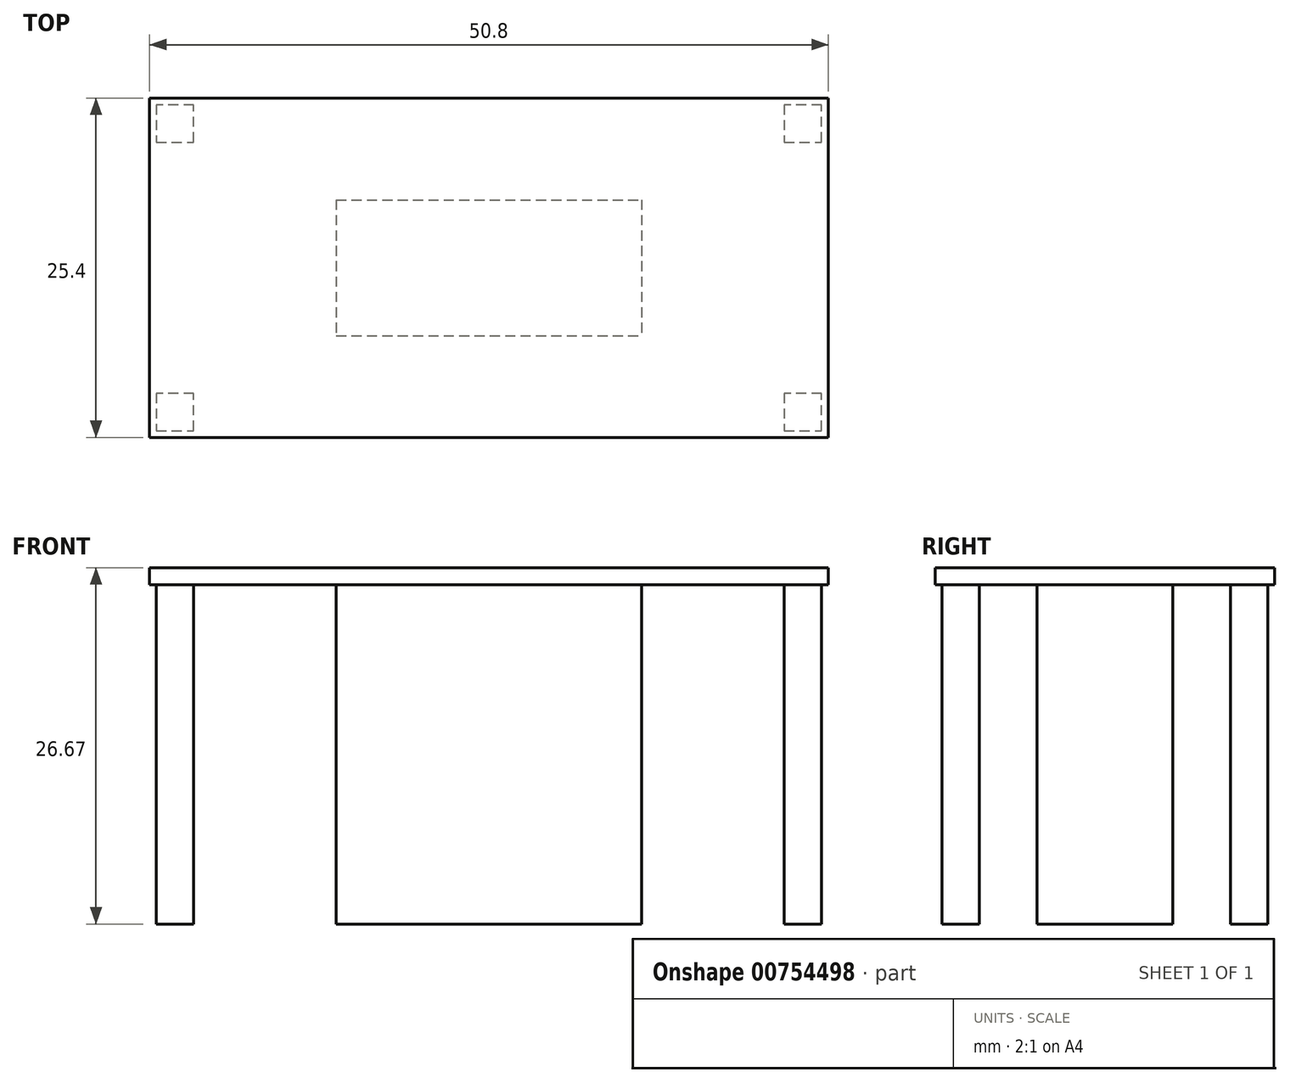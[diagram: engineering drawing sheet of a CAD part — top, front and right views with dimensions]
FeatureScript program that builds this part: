
annotation { "Feature Type Name" : "Feature", "Feature Type Description" : "" }
export const myFeature = defineFeature(function(context is Context, id is Id, definition is map)
    precondition{}
    {
        {
            var Q0;
            Q0=qCreatedBy(makeId("Top.planeOp"),FACE);
            var sketch = newSketch(context, id + "F0", { "sketchPlane" : qUnion([Q0])});
            skLineSegment(sketch, "E0.bottom", {"start": v(25.4, -12.7) * mm, "end": v(-25.4, -12.7) * mm});
            skLineSegment(sketch, "E0.top", {"start": v(25.4, 12.7) * mm, "end": v(-25.4, 12.7) * mm});
            skLineSegment(sketch, "E0.left", {"start": v(25.4, -12.7) * mm, "end": v(25.4, 12.7) * mm});
            skLineSegment(sketch, "E0.right", {"start": v(-25.4, -12.7) * mm, "end": v(-25.4, 12.7) * mm});
            skPoint(sketch, "E0.middle", {"position": v(0, 0) * mm});
            skLineSegment(sketch, "E1.bottom", {"start": v(-25.4, 12.7) * mm, "end": v(-21.6, 12.7) * mm});
            skLineSegment(sketch, "E1.top", {"start": v(-25.4, 8.9) * mm, "end": v(-21.59, 8.9) * mm});
            skLineSegment(sketch, "E1.left", {"start": v(-25.4, 12.7) * mm, "end": v(-25.4, 8.9) * mm});
            skLineSegment(sketch, "E1.right", {"start": v(-21.6, 12.7) * mm, "end": v(-21.6, 8.9) * mm});
            skLineSegment(sketch, "E2.bottom", {"start": v(-25.4, -12.7) * mm, "end": v(-21.6, -12.7) * mm});
            skLineSegment(sketch, "E2.top", {"start": v(-25.4, -8.89) * mm, "end": v(-21.6, -8.89) * mm});
            skLineSegment(sketch, "E2.left", {"start": v(-25.4, -12.7) * mm, "end": v(-25.4, -8.89) * mm});
            skLineSegment(sketch, "E2.right", {"start": v(-21.6, -12.7) * mm, "end": v(-21.6, -8.89) * mm});
            skLineSegment(sketch, "E3.bottom", {"start": v(25.4, -12.7) * mm, "end": v(21.59, -12.7) * mm});
            skLineSegment(sketch, "E3.top", {"start": v(25.4, -8.89) * mm, "end": v(21.59, -8.89) * mm});
            skLineSegment(sketch, "E3.left", {"start": v(25.4, -12.7) * mm, "end": v(25.4, -8.89) * mm});
            skLineSegment(sketch, "E3.right", {"start": v(21.59, -12.7) * mm, "end": v(21.59, -8.89) * mm});
            skLineSegment(sketch, "E4.bottom", {"start": v(25.4, 12.7) * mm, "end": v(21.59, 12.7) * mm});
            skLineSegment(sketch, "E4.top", {"start": v(25.4, 8.9) * mm, "end": v(21.6, 8.9) * mm});
            skLineSegment(sketch, "E4.left", {"start": v(25.4, 12.7) * mm, "end": v(25.4, 8.9) * mm});
            skLineSegment(sketch, "E4.right", {"start": v(21.59, 12.7) * mm, "end": v(21.59, 8.9) * mm});
            skLineSegment(sketch, "E5.bottom", {"start": v(-11.43, 5.08) * mm, "end": v(11.43, 5.08) * mm});
            skLineSegment(sketch, "E5.top", {"start": v(-11.43, -5.08) * mm, "end": v(11.43, -5.08) * mm});
            skLineSegment(sketch, "E5.left", {"start": v(-11.43, 5.08) * mm, "end": v(-11.43, -5.08) * mm});
            skLineSegment(sketch, "E5.right", {"start": v(11.43, 5.08) * mm, "end": v(11.43, -5.08) * mm});
            skSolve(sketch);
        }
        {
            var Q0;
            {var subQ4=sQuery(id+"F0.wireOp",EDGE,"E2.top");Q0=makeQuery(id+"F0.imprint","IMPRINT",FACE,{"disambiguationData":[TD([[makeQuery(id+"F0.imprint","IMPRINT",EDGE,{"derivedFrom":subQ4}),-1.0]])]});}
            var sketch = newSketch(context, id + "F1", { "sketchPlane" : qUnion([Q0])});
            skLineSegment(sketch, "E6.0", {"start": v(-24.9, -12.2) * mm, "end": v(-22.1, -12.2) * mm});
            skLineSegment(sketch, "E6.1", {"start": v(-24.9, -9.4) * mm, "end": v(-24.9, -12.2) * mm});
            skLineSegment(sketch, "E6.2", {"start": v(-22.1, -9.4) * mm, "end": v(-24.9, -9.4) * mm});
            skLineSegment(sketch, "E6.3", {"start": v(-22.1, -12.2) * mm, "end": v(-22.1, -9.4) * mm});
            skLineSegment(sketch, "E7.0", {"start": v(22.1, -9.4) * mm, "end": v(22.1, -12.2) * mm});
            skLineSegment(sketch, "E7.1", {"start": v(24.9, -9.4) * mm, "end": v(22.1, -9.4) * mm});
            skLineSegment(sketch, "E7.2", {"start": v(24.9, -12.2) * mm, "end": v(24.9, -9.4) * mm});
            skLineSegment(sketch, "E7.3", {"start": v(22.1, -12.2) * mm, "end": v(24.9, -12.2) * mm});
            skLineSegment(sketch, "E8.0", {"start": v(24.9, 9.4) * mm, "end": v(24.9, 12.2) * mm});
            skLineSegment(sketch, "E8.1", {"start": v(22.1, 9.4) * mm, "end": v(24.9, 9.4) * mm});
            skLineSegment(sketch, "E8.2", {"start": v(22.1, 12.2) * mm, "end": v(22.1, 9.4) * mm});
            skLineSegment(sketch, "E8.3", {"start": v(24.9, 12.2) * mm, "end": v(22.1, 12.2) * mm});
            skLineSegment(sketch, "E9.0", {"start": v(-22.1, 12.2) * mm, "end": v(-24.9, 12.2) * mm});
            skLineSegment(sketch, "E9.1", {"start": v(-22.1, 9.4) * mm, "end": v(-22.1, 12.2) * mm});
            skLineSegment(sketch, "E9.2", {"start": v(-24.9, 9.4) * mm, "end": v(-22.1, 9.4) * mm});
            skLineSegment(sketch, "E9.3", {"start": v(-24.9, 12.2) * mm, "end": v(-24.9, 9.4) * mm});
            skSolve(sketch);
        }
        {
            var Q0;
            Q0 = qSketchRegion(id + "F1", true);
            var Q1;
            Q1=makeQuery(id+"F0.imprint","IMPRINT",FACE,{"disambiguationData":[TD([[makeQuery(id+"F0.imprint","IMPRINT",EDGE,{"derivedFrom":sQuery(id+"F0.wireOp",EDGE,"E5.bottom")}),-1.0]])]});
            extrude(context, id + "F2", {"entities" : qUnion([Q0, Q1]), "oppositeDirection" : true, "depth" : 25.4 * mm, "offsetDistance" : 25.4 * mm});
        }
        {
            var Q0;
            {var subQ5=sQuery(id+"F0.wireOp",EDGE,"E1.top");var subQ7=makeQuery(id+"F0.imprint","IMPRINT",EDGE,{"derivedFrom":subQ5});var subQ9=sQuery(id+"F0.wireOp",EDGE,"E3.top");var subQ10=makeQuery(id+"F0.imprint","IMPRINT",EDGE,{"derivedFrom":subQ9});var subQ17=sQuery(id+"F0.wireOp",EDGE,"E2.top");var subQ18=makeQuery(id+"F0.imprint","IMPRINT",EDGE,{"derivedFrom":subQ17});var subQ24=sQuery(id+"F0.wireOp",EDGE,"E4.top");var subQ27=makeQuery(id+"F0.imprint","IMPRINT",EDGE,{"derivedFrom":subQ24});Q0=qUnion([makeQuery(id+"F0.imprint","IMPRINT",FACE,{"disambiguationData":[TD([[subQ27,-1.0]])]}),makeQuery(id+"F0.imprint","IMPRINT",FACE,{"disambiguationData":[TD([[subQ10,1.0]])]}),makeQuery(id+"F0.imprint","IMPRINT",FACE,{"disambiguationData":[TD([[subQ18,-1.0]])]}),makeQuery(id+"F0.imprint","IMPRINT",FACE,{"disambiguationData":[TD([[subQ7,-1.0]])]}),makeQuery(id+"F0.imprint","IMPRINT",FACE,{"disambiguationData":[TD([[subQ7,1.0]])]})]);}
            var Q1;
            Q1=makeQuery(id+"F0.imprint","IMPRINT",FACE,{"disambiguationData":[TD([[makeQuery(id+"F0.imprint","IMPRINT",EDGE,{"derivedFrom":sQuery(id+"F0.wireOp",EDGE,"E5.bottom")}),-1.0]])]});
            extrude(context, id + "F3", {"entities" : qUnion([Q0, Q1]), "depth" : 1.27 * mm, "offsetDistance" : 25.4 * mm});
        }
    });
